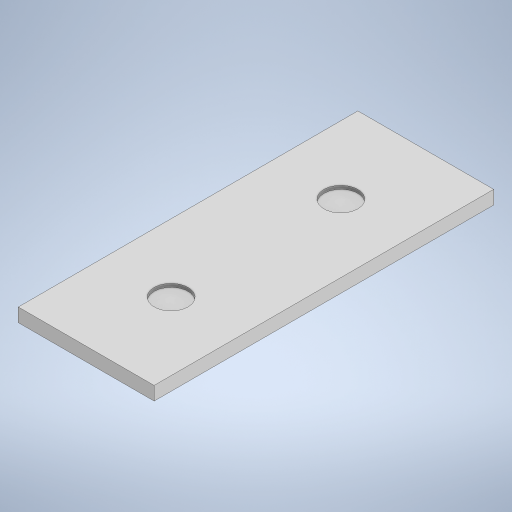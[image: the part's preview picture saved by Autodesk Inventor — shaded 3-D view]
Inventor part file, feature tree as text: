
AUTODESK INVENTOR PART (.ipt)
format: ipt  version: 2024 (Build 280153000, 153)  size: 220,672 bytes
history: native  units: in
note: dims shown in document units (in); Inventor stores cm internally (conversion verified against a paired STEP export)
features: extrude x2, sketch x2
ambient origin geometry x8: Origin, YZ Plane, XZ Plane, XY Plane, X Axis, Y Axis, Z Axis, Center Point
bodies: Solid1 (feature_tree)
feature tree (4):
  extrude  "Extrusion1"  Depth=1.9685in
  extrude  "Extrusion2"  Depth=0.0197in
  sketch  "Sketch1"  dims[d0=0.7874in d1=1.9685in]
  sketch  "Sketch2"  dims[d2=0.0787in d3=0.0in d4=0.1969in d5=0.1969in d6=0.0197in d7=0.0in]
